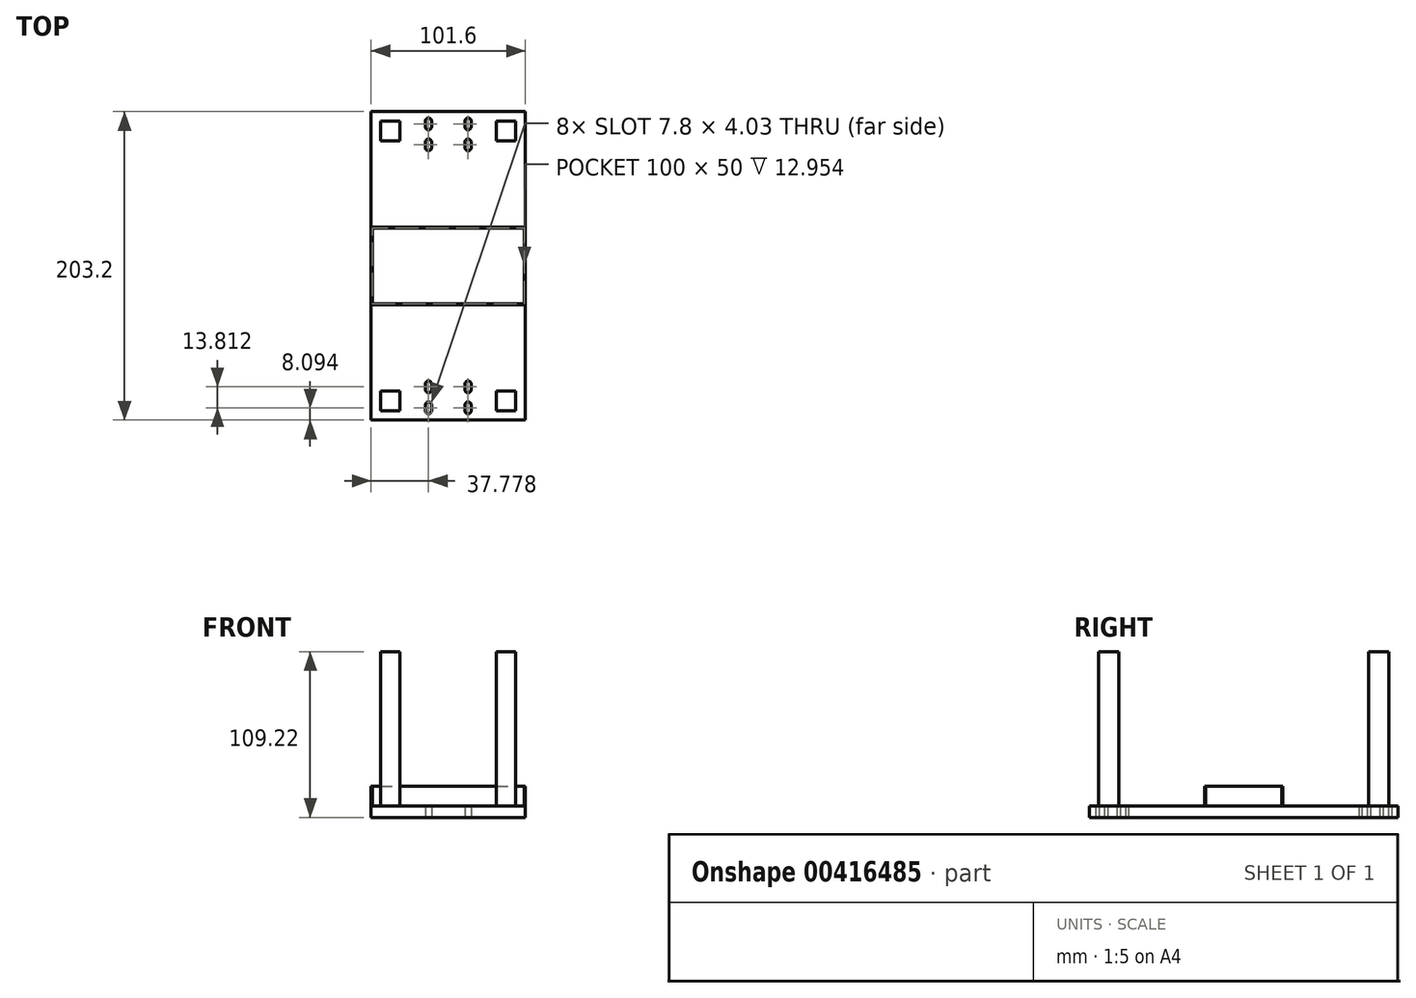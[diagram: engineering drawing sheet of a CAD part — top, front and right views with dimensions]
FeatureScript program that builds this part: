
annotation { "Feature Type Name" : "Feature", "Feature Type Description" : "" }
export const myFeature = defineFeature(function(context is Context, id is Id, definition is map)
    precondition{}
    {
        {
            var Q0;
            Q0=qCreatedBy(makeId("Top.planeOp"),FACE);
            var sketch = newSketch(context, id + "F0", { "sketchPlane" : qUnion([Q0])});
            skLineSegment(sketch, "E0.bottom", {"start": v(-50.8, 101.6) * mm, "end": v(50.8, 101.6) * mm});
            skLineSegment(sketch, "E0.top", {"start": v(-50.8, -101.6) * mm, "end": v(50.8, -101.6) * mm});
            skLineSegment(sketch, "E0.left", {"start": v(-50.8, 101.6) * mm, "end": v(-50.8, -101.6) * mm});
            skLineSegment(sketch, "E0.right", {"start": v(50.8, 101.6) * mm, "end": v(50.8, -101.6) * mm});
            skPoint(sketch, "E0.middle", {"position": v(0, 0) * mm});
            skSolve(sketch);
        }
        {
            var Q0;
            Q0 = qSketchRegion(id + "F0", true);
            extrude(context, id + "F1", {"entities" : qUnion([Q0]), "depth" : 7.62 * mm});
        }
        {
            var Q0;
            Q0=qCreatedBy(makeId("Top.planeOp"),FACE);
            var sketch = newSketch(context, id + "F2", { "sketchPlane" : qUnion([Q0])});
            skLineSegment(sketch, "E1.top", {"start": v(-19, -101.6) * mm, "end": v(19, -101.6) * mm});
            skArc(sketch, "E2", {"start": v(-14.99, -81.42) * mm, "mid": v(-13.08, -83.6) * mm, "end": v(-11, -81.58) * mm});
            skArc(sketch, "E3", {"start": v(-11.05, -77.84) * mm, "mid": v(-13.03, -75.8) * mm, "end": v(-15.04, -77.82) * mm});
            skLineSegment(sketch, "E4", {"start": v(-11.05, -77.84) * mm, "end": v(-11, -81.58) * mm});
            skLineSegment(sketch, "E5", {"start": v(-15.04, -77.82) * mm, "end": v(-14.99, -81.42) * mm});
            skLineSegment(sketch, "E6.MirrorCS", {"start": v(-11.05, -95.36) * mm, "end": v(-11, -91.62) * mm});
            skLineSegment(sketch, "E7.MirrorCS", {"start": v(-15.04, -95.38) * mm, "end": v(-14.99, -91.78) * mm});
            skArc(sketch, "E8.MirrorCS", {"start": v(-14.99, -91.78) * mm, "mid": v(-13.08, -89.6) * mm, "end": v(-11, -91.62) * mm});
            skArc(sketch, "E9.MirrorCS", {"start": v(-11.05, -95.36) * mm, "mid": v(-13.03, -97.4) * mm, "end": v(-15.04, -95.38) * mm});
            skLineSegment(sketch, "E10.MirrorCS", {"start": v(11.05, -77.84) * mm, "end": v(11, -81.58) * mm});
            skLineSegment(sketch, "E11.MirrorCS", {"start": v(15.04, -77.82) * mm, "end": v(14.99, -81.42) * mm});
            skArc(sketch, "E12.MirrorCS", {"start": v(14.99, -81.42) * mm, "mid": v(13.08, -83.6) * mm, "end": v(11, -81.58) * mm});
            skArc(sketch, "E13.MirrorCS", {"start": v(11.05, -77.84) * mm, "mid": v(13.03, -75.8) * mm, "end": v(15.04, -77.82) * mm});
            skArc(sketch, "E14.MirrorCS", {"start": v(11.05, -95.36) * mm, "mid": v(13.03, -97.4) * mm, "end": v(15.04, -95.38) * mm});
            skLineSegment(sketch, "E15.MirrorCS", {"start": v(11.05, -95.36) * mm, "end": v(11, -91.62) * mm});
            skArc(sketch, "E16.MirrorCS", {"start": v(14.99, -91.78) * mm, "mid": v(13.08, -89.6) * mm, "end": v(11, -91.62) * mm});
            skLineSegment(sketch, "E17", {"start": v(14.99, -91.78) * mm, "end": v(15.04, -95.38) * mm});
            skLineSegment(sketch, "E18.MirrorCS", {"start": v(11.05, 95.36) * mm, "end": v(11, 91.62) * mm});
            skArc(sketch, "E19.MirrorCS", {"start": v(-11.05, 95.36) * mm, "mid": v(-13.03, 97.4) * mm, "end": v(-15.04, 95.38) * mm});
            skLineSegment(sketch, "E20.MirrorCS", {"start": v(-11.05, 77.84) * mm, "end": v(-11, 81.58) * mm});
            skLineSegment(sketch, "E21.MirrorCS", {"start": v(15.04, 77.82) * mm, "end": v(14.99, 81.42) * mm});
            skLineSegment(sketch, "E22.MirrorCS", {"start": v(11.05, 77.84) * mm, "end": v(11, 81.58) * mm});
            skArc(sketch, "E23.MirrorCS", {"start": v(11.05, 77.84) * mm, "mid": v(13.03, 75.8) * mm, "end": v(15.04, 77.82) * mm});
            skArc(sketch, "E24.MirrorCS", {"start": v(-14.99, 81.42) * mm, "mid": v(-13.08, 83.6) * mm, "end": v(-11, 81.58) * mm});
            skArc(sketch, "E25.MirrorCS", {"start": v(-11.05, 77.84) * mm, "mid": v(-13.03, 75.8) * mm, "end": v(-15.04, 77.82) * mm});
            skArc(sketch, "E26.MirrorCS", {"start": v(14.99, 91.78) * mm, "mid": v(13.08, 89.6) * mm, "end": v(11, 91.62) * mm});
            skLineSegment(sketch, "E27.MirrorCS", {"start": v(-15.04, 95.38) * mm, "end": v(-14.99, 91.78) * mm});
            skArc(sketch, "E28.MirrorCS", {"start": v(11.05, 95.36) * mm, "mid": v(13.03, 97.4) * mm, "end": v(15.04, 95.38) * mm});
            skLineSegment(sketch, "E29.MirrorCS", {"start": v(-15.04, 77.82) * mm, "end": v(-14.99, 81.42) * mm});
            skArc(sketch, "E30.MirrorCS", {"start": v(-14.99, 91.78) * mm, "mid": v(-13.08, 89.6) * mm, "end": v(-11, 91.62) * mm});
            skLineSegment(sketch, "E31.MirrorCS", {"start": v(14.99, 91.78) * mm, "end": v(15.04, 95.38) * mm});
            skLineSegment(sketch, "E32.MirrorCS", {"start": v(-11.05, 95.36) * mm, "end": v(-11, 91.62) * mm});
            skArc(sketch, "E33.MirrorCS", {"start": v(14.99, 81.42) * mm, "mid": v(13.08, 83.6) * mm, "end": v(11, 81.58) * mm});
            skSolve(sketch);
        }
        {
            var Q0;
            Q0 = qSketchRegion(id + "F2", true);
            extrude(context, id + "F3", {"entities" : qUnion([Q0]), "operationType" : NewBodyOperationType.REMOVE, "oppositeDirection" : true, "depth" : -25.4 * mm});
        }
        {
            var Q0;
            Q0=makeQuery(id+"F1.opExtrude","CAP_FACE",FACE,{"disambiguationData":[OSD([sQuery(id+"F0.wireOp",EDGE,"E0.bottom"),sQuery(id+"F0.wireOp",EDGE,"E0.top"),sQuery(id+"F0.wireOp",EDGE,"E0.left"),sQuery(id+"F0.wireOp",EDGE,"E0.right")])],"isStart":false});
            var sketch = newSketch(context, id + "F4", { "sketchPlane" : qUnion([Q0])});
            skLineSegment(sketch, "E34.bottom", {"start": v(31.75, 95.45) * mm, "end": v(44.45, 95.45) * mm});
            skLineSegment(sketch, "E34.top", {"start": v(31.75, 82.35) * mm, "end": v(44.45, 82.35) * mm});
            skLineSegment(sketch, "E34.left", {"start": v(31.75, 95.45) * mm, "end": v(31.75, 82.35) * mm});
            skLineSegment(sketch, "E34.right", {"start": v(44.45, 95.45) * mm, "end": v(44.45, 82.35) * mm});
            skPoint(sketch, "E34.middle", {"position": v(38.1, 88.9) * mm});
            skLineSegment(sketch, "E35.MirrorCS", {"start": v(-31.75, 82.35) * mm, "end": v(-44.45, 82.35) * mm});
            skLineSegment(sketch, "E36.MirrorCS", {"start": v(-44.45, 95.45) * mm, "end": v(-44.45, 82.35) * mm});
            skLineSegment(sketch, "E37.MirrorCS", {"start": v(-31.75, 95.45) * mm, "end": v(-31.75, 82.35) * mm});
            skLineSegment(sketch, "E38.MirrorCS", {"start": v(-31.75, 95.45) * mm, "end": v(-44.45, 95.45) * mm});
            skLineSegment(sketch, "E39.MirrorCS", {"start": v(31.75, -95.45) * mm, "end": v(31.75, -82.35) * mm});
            skLineSegment(sketch, "E40.MirrorCS", {"start": v(31.75, -82.35) * mm, "end": v(44.45, -82.35) * mm});
            skLineSegment(sketch, "E41.MirrorCS", {"start": v(44.45, -95.45) * mm, "end": v(44.45, -82.35) * mm});
            skLineSegment(sketch, "E42.MirrorCS", {"start": v(31.75, -95.45) * mm, "end": v(44.45, -95.45) * mm});
            skLineSegment(sketch, "E43.MirrorCS", {"start": v(-31.75, -95.45) * mm, "end": v(-31.75, -82.35) * mm});
            skLineSegment(sketch, "E44.MirrorCS", {"start": v(-31.75, -95.45) * mm, "end": v(-44.45, -95.45) * mm});
            skLineSegment(sketch, "E45.MirrorCS", {"start": v(-31.75, -82.35) * mm, "end": v(-44.45, -82.35) * mm});
            skLineSegment(sketch, "E46.MirrorCS", {"start": v(-44.45, -95.45) * mm, "end": v(-44.45, -82.35) * mm});
            skSolve(sketch);
        }
        {
            var Q0;
            Q0 = qSketchRegion(id + "F4", true);
            extrude(context, id + "F5", {"entities" : qUnion([Q0]), "operationType" : NewBodyOperationType.ADD, "depth" : 101.6 * mm});
        }
        {
            var Q0;
            Q0=makeQuery(id+"F1.opExtrude","CAP_FACE",FACE,{"disambiguationData":[OSD([sQuery(id+"F0.wireOp",EDGE,"E0.bottom"),sQuery(id+"F0.wireOp",EDGE,"E0.top"),sQuery(id+"F0.wireOp",EDGE,"E0.left"),sQuery(id+"F0.wireOp",EDGE,"E0.right")])],"isStart":false});
            var sketch = newSketch(context, id + "F6", { "sketchPlane" : qUnion([Q0])});
            skLineSegment(sketch, "E47.bottom", {"start": v(-50, 25) * mm, "end": v(50, 25) * mm});
            skLineSegment(sketch, "E47.top", {"start": v(-50, -25) * mm, "end": v(50, -25) * mm});
            skLineSegment(sketch, "E47.left", {"start": v(-50, 25) * mm, "end": v(-50, -25) * mm});
            skLineSegment(sketch, "E47.right", {"start": v(50, 25) * mm, "end": v(50, -25) * mm});
            skPoint(sketch, "E47.middle", {"position": v(0, 0) * mm});
            skLineSegment(sketch, "E48.0", {"start": v(-50, 25.58) * mm, "end": v(50, 25.58) * mm});
            skLineSegment(sketch, "E49.0", {"start": v(-50, -25.58) * mm, "end": v(50, -25.58) * mm});
            skLineSegment(sketch, "E50.0", {"start": v(50.76, 25) * mm, "end": v(50.76, -25) * mm});
            skLineSegment(sketch, "E51.0", {"start": v(-50.78, 25) * mm, "end": v(-50.78, -25) * mm});
            skLineSegment(sketch, "E52", {"start": v(50, 25.58) * mm, "end": v(50.76, 25) * mm});
            skLineSegment(sketch, "E53", {"start": v(-50.78, 25) * mm, "end": v(-50, 25.58) * mm});
            skLineSegment(sketch, "E54", {"start": v(-50.78, -25) * mm, "end": v(-50, -25.58) * mm});
            skLineSegment(sketch, "E55", {"start": v(50, -25.58) * mm, "end": v(50.76, -25) * mm});
            skSolve(sketch);
        }
        {
            var Q0;
            Q0 = qSketchRegion(id + "F6", true);
            extrude(context, id + "F7", {"entities" : qUnion([Q0]), "operationType" : NewBodyOperationType.ADD, "depth" : 12.95 * mm});
        }
    });
